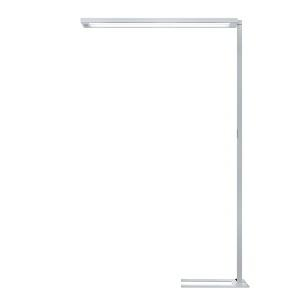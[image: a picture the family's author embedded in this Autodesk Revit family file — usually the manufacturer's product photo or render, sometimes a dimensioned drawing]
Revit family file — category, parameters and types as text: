
# Revit family: lavigo_-_dps_18000_vtl_r_g2_00801139_36ca
name_source: partatom
category: Lighting Fixtures
units: mm (PartAtom-declared; Revit-internal decimal feet)

## family parameters
Cut with Voids When Loaded = No
Host = Face
Light Source = No
Part Type = Normal
Room Calculation Point = No
Round Connector Dimension = Use Diameter
Shared = No

## types (1)
- LAVIGO - DPS 18000/VTL/R/G2 (1 x LED VTL, 18550 lm, 3000-6500K)
    Apparent Load = 128 VA
    Approval mark = CE
    CIE Flux Codes = 60 87 97 9 100
    Color Rendering = 80-89
    Color Temperature = 3000-6500K
    Control Gear = Electronic ballast
    Default Elevation = 1800 mm
    Description = DPS 18000/VTL/R/G2|Free-standing luminaire|light source: LED  3000-6500 K  Energy efficiency category A/A+/A++|LED  4000 K 4000 K Energy efficiency category A/A+/A++|work equipment: Electronic ballast DALI|connected load: 220-240 V, 50/60 Hz|Power consumption: approx. 128 W|standby: approx. 0,50|power factor: approx. 0,966|luminous flux: 18850 lm|luminous efficacy: 147 lm/W|light distribution: Direct/indirect|direct ratio: approx. 9 %|color rendering index (CRI): >= 80|technology: Presence and daylight sensor control (PIR)|operation: Multi-function switch|luminaire body|material: Steel/plastic|surface: Powder coatet|colour: Silver metallic|lamp cover: Polycarbonate (PC), Clear, Structured|tubular section|material: Steel tube|surface: Powder-coated|Form: Tubular section upright|colour of tubular section: Silver metallic|luminaire base|Form: C-form flat|weight (net): approx. 15.4 kg|mains lead: 3.00 m Mains plug CEE 7/VII|Fastening: Floor standing base|decorative contrast side parts: Flint grey|glare control: Prism aperture|luminance(L65): <= 2800 cd/m|unified glare rating(4H 8H): <=  16|special features: Luminaire head detachable, Cradle to Cradle Certified TM, Direct light component with edge light and light-guide technology for homogenous light exit, Flicker-free, Indirect light component biodynamic light VTL, direct light component neutral working light, Integrated light and presence sensor PIR, Integrated light management for biodynamic light VTL, Retrofittable with TALK module, Separated, direct and indirect light individually adjustable|
    Frequency = 50 Hz
    Height = 36 mm
    Lamp = 1 x LED VTL
    Lamp Light Flux = 18550 lm
    Lamp count = 1
    Length = 1265 mm
    Luminous efficacy = 145 lm/W
    Manufacturer = Waldmann
    ModVariant = No
    Model = 00801139
    Mounting Place = Floor
    Mounting Type = Freestanding
    Number of Poles = 1
    OnlyDefault = Yes
    Power Factor = 1
    Product Name = LAVIGO - DPS 18000/VTL/R/G2
    Product group = Free standing luminaire
    ProductGroupID = 13
    Protection Class = Protection class I
    Protection Degree = IP 20
    RLX_Detail_Level = 1
    RLX_Emergency_Light_Flux = 0 lm
    RLX_Emergency_Type = 0
    RLX_Emergency_Type_DB = No
    RlxData = <blob elided: 30841 chars, md5=bbf8e235>
    Socket = socket
    Standby Power = 0 W
    System Light Flux = 18550 lm
    System Power = 128 W
    Type Comments = Product without accessories
    Type Image = 121763000-00712217.jpg
    URL = http://relux.com
    VarID = ---
    Voltage = 230 V
    Voltage Range = 220-240 V
    Weight = 0.00 kg
    Width = 201 mm

## geometry (parser evidence)
native form markers: Blend x4, Sweep x14
no freeform markers — native parametric forms only
